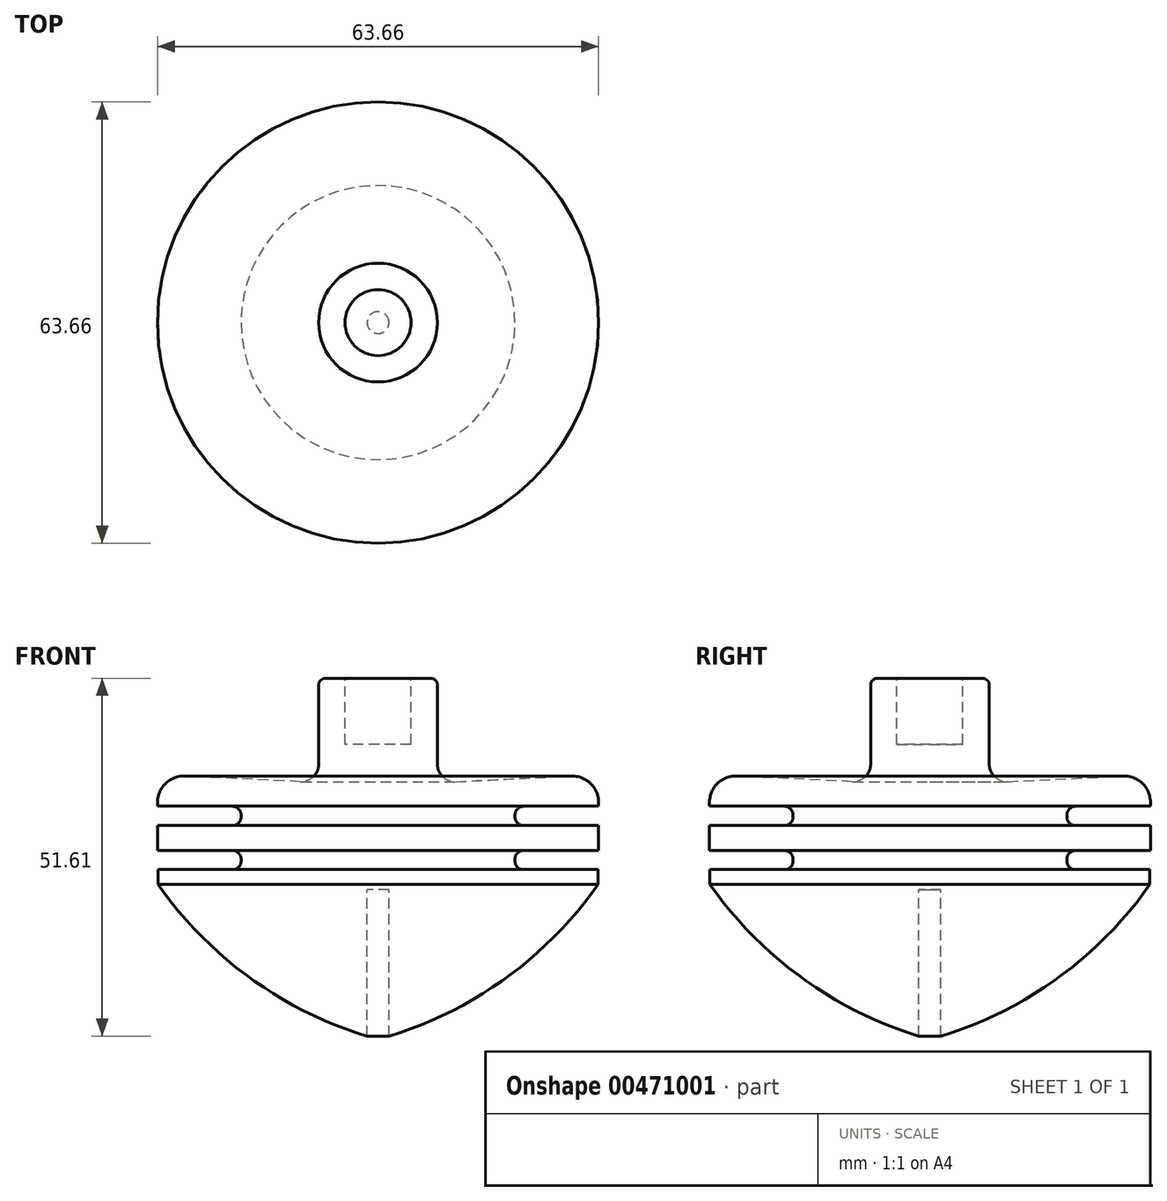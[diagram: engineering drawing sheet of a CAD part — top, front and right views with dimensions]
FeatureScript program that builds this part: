
annotation { "Feature Type Name" : "Feature", "Feature Type Description" : "" }
export const myFeature = defineFeature(function(context is Context, id is Id, definition is map)
    precondition{}
    {
        {
            var Q0;
            Q0=qCreatedBy(makeId("Front.planeOp"),FACE);
            var sketch = newSketch(context, id + "F0", { "sketchPlane" : qUnion([Q0])});
            skPoint(sketch, "E0", {"position": v(19.76, 24.45) * mm});
            skPoint(sketch, "E1", {"position": v(19.76, 27.24) * mm});
            skPoint(sketch, "E2", {"position": v(8.56, 37.03) * mm});
            skPoint(sketch, "E3", {"position": v(0, 52.07) * mm});
            skLineSegment(sketch, "E4", {"start": v(31.75, 24.48) * mm, "end": v(21.04, 24.45) * mm});
            skLineSegment(sketch, "E5", {"start": v(21.03, 27.24) * mm, "end": v(31.83, 27.24) * mm});
            skLineSegment(sketch, "E6", {"start": v(27.83, 37.98) * mm, "end": v(11.22, 37.16) * mm});
            skLineSegment(sketch, "E7", {"start": v(7.62, 52.07) * mm, "end": v(0, 52.07) * mm});
            skLineSegment(sketch, "E8", {"start": v(19.76, 25.72) * mm, "end": v(19.76, 25.97) * mm});
            skLineSegment(sketch, "E9", {"start": v(8.56, 39.7) * mm, "end": v(8.56, 51.13) * mm});
            skLineSegment(sketch, "E10", {"start": v(0, 52.07) * mm, "end": v(0, 0) * mm});
            skPoint(sketch, "E11", {"position": v(19.76, 30.82) * mm});
            skPoint(sketch, "E12", {"position": v(19.76, 33.61) * mm});
            skLineSegment(sketch, "E13", {"start": v(31.83, 30.82) * mm, "end": v(21.03, 30.82) * mm});
            skLineSegment(sketch, "E14", {"start": v(19.76, 32.1) * mm, "end": v(19.76, 32.34) * mm});
            skLineSegment(sketch, "E15", {"start": v(21.03, 33.61) * mm, "end": v(31.83, 33.61) * mm});
            skArc(sketch, "E16.filletArc", {"start": v(8.56, 39.7) * mm, "mid": v(9.35, 37.86) * mm, "end": v(11.22, 37.16) * mm});
            skArc(sketch, "E17.filletArc", {"start": v(8.56, 51.13) * mm, "mid": v(8.29, 51.8) * mm, "end": v(7.62, 52.07) * mm});
            skArc(sketch, "E18.filletArc", {"start": v(21.03, 33.61) * mm, "mid": v(20.13, 33.24) * mm, "end": v(19.76, 32.34) * mm});
            skArc(sketch, "E19.filletArc", {"start": v(19.76, 32.1) * mm, "mid": v(20.13, 31.2) * mm, "end": v(21.03, 30.82) * mm});
            skArc(sketch, "E20.filletArc", {"start": v(21.03, 27.24) * mm, "mid": v(20.13, 26.87) * mm, "end": v(19.76, 25.97) * mm});
            skArc(sketch, "E21.filletArc", {"start": v(19.76, 25.72) * mm, "mid": v(20.14, 24.82) * mm, "end": v(21.04, 24.45) * mm});
            skLineSegment(sketch, "E22", {"start": v(31.75, 24.48) * mm, "end": v(31.75, 22.36) * mm});
            skArc(sketch, "E23", {"start": v(0, 0) * mm, "mid": v(17.84, 8.4) * mm, "end": v(31.75, 22.36) * mm});
            skLineSegment(sketch, "E24", {"start": v(31.83, 27.24) * mm, "end": v(31.83, 30.82) * mm});
            skLineSegment(sketch, "E25", {"start": v(31.83, 33.61) * mm, "end": v(31.83, 34.17) * mm});
            skArc(sketch, "E26.filletArc", {"start": v(31.83, 34.17) * mm, "mid": v(30.64, 36.93) * mm, "end": v(27.83, 37.98) * mm});
            skLineSegment(sketch, "E27", {"start": v(0, 52.07) * mm, "end": v(4.76, 52.07) * mm});
            skLineSegment(sketch, "E28", {"start": v(4.76, 52.07) * mm, "end": v(4.76, 42.55) * mm});
            skLineSegment(sketch, "E29", {"start": v(4.76, 42.55) * mm, "end": v(0, 42.55) * mm});
            skLineSegment(sketch, "E30", {"start": v(0, 0) * mm, "end": v(0, 21.59) * mm});
            skLineSegment(sketch, "E31", {"start": v(0, 21.59) * mm, "end": v(1.59, 21.59) * mm});
            skLineSegment(sketch, "E32", {"start": v(1.59, 21.59) * mm, "end": v(1.59, 0.46) * mm});
            skSolve(sketch);
        }
        {
            var Q0;
            Q0=makeQuery(id+"F0.imprint","IMPRINT",FACE,{"disambiguationData":[TD([[makeQuery(id+"F0.imprint","IMPRINT",EDGE,{"derivedFrom":sQuery(id+"F0.wireOp",EDGE,"E4")}),1.0]])]});
            var Q1;
            Q1=sQuery(id+"F0.wireOp",EDGE,"E10");
            revolve(context, id + "F1", {"entities" : qUnion([Q0]), "axis" : qUnion([Q1]), "revolveType" : RevolveType.FULL});
        }
    });
